# Revit family: Atdec-Bracket-TH-VWVP-
name_source: partatom
category: Generic Models
revit_build: Autodesk Revit 2016 (Build: 20150220_1215(x64)
units: mm (PartAtom-declared; Revit-internal decimal feet)

## family parameters
Can host rebar = No
Cut with Voids When Loaded = No
Host = Face
Part Type = Normal
Room Calculation Point = No
Round Connector Dimension = Use Diameter
Shared = No

## types (1)
- TH-VWVP
    Assembly Code = E1010800
    Colour Options = Black
    Default Elevation = 1219 mm
    Description = Video wall portrait display brackets (set of 2)
    Flat screen maximum supported weight = 165kg (363lb)
    Manufacturer = Atdec
    Master Carton Dimensions = 1021mm (40.2") Lenght, 166mm (6.5") Width, 309mm (12.2") Height
    Material = Steel
    Maximum distance from wall (mm) = 44.5mm (1.75")
    Minimum distance from wall (mm) = 44.5mm (1.75")
    Model = TH-VWVP
    Pan Adjustment = -
    Product Family = Wall Mount Rail
    Product Information Link = https://www.atdec.com.au
    Range of Motion = Fixed Angle
    Security feature = Can be secured with padlock (not included)
    Single Unit Dimensions = 1005mm (39.6") Lenght, 163mm (6.4") Width, 75mm (2.95") Height
    Single units per master pack = 4
    Tilt Adjustment = -
    UPC Code = 881493009462
    URL = www.atdec.com.au
    Universal Height (mm) = From 100 to 600
    Universal Width (mm) = Flexible
    VESA mounting hole pattern,mm = -
    Warranty = 10 years
    Weight, Master Carton = 25.5kg (56.2lb)
    Weight, Single Unit = 6.3kg (13.8lb)

## geometry (parser evidence)
native form markers: Sweep x2
no freeform markers — native parametric forms only
